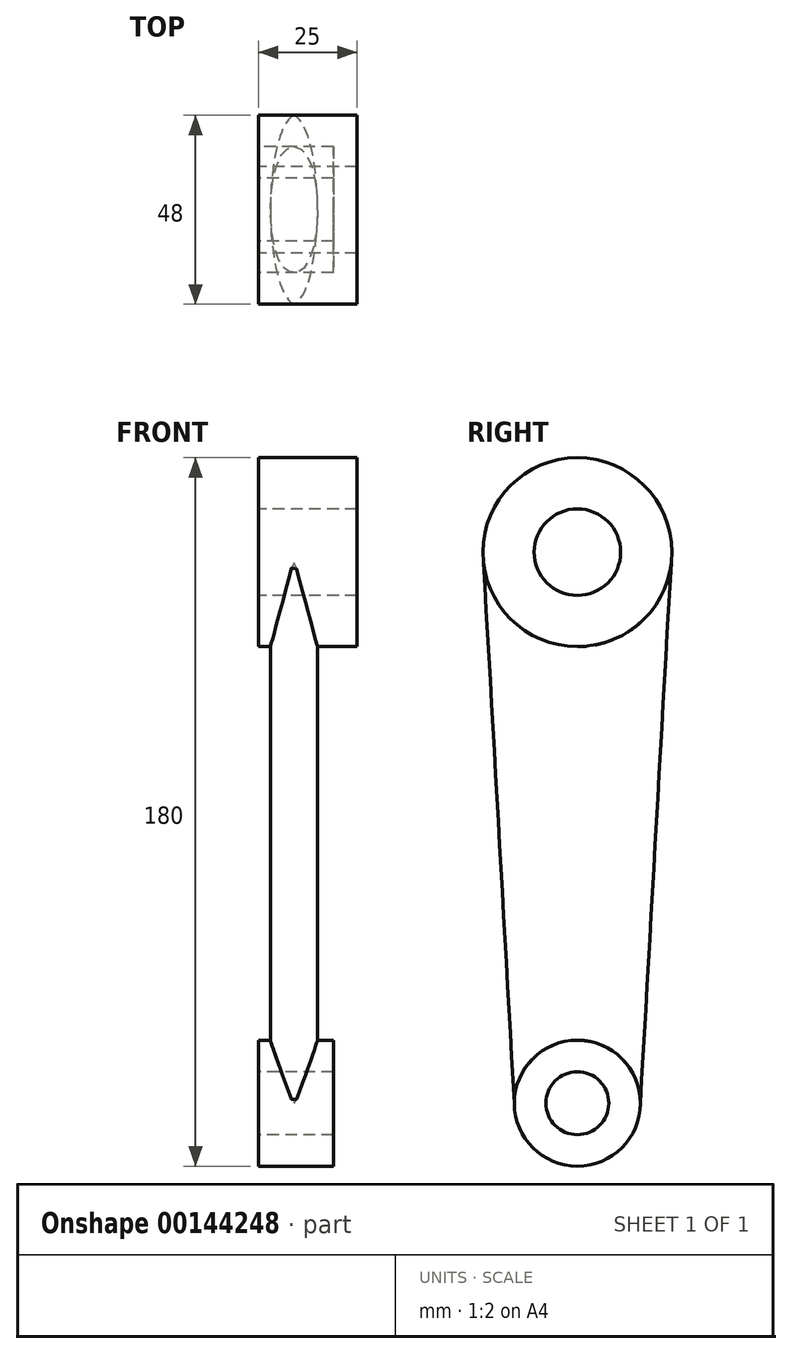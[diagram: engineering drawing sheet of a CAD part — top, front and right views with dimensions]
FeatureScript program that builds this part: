
annotation { "Feature Type Name" : "Feature", "Feature Type Description" : "" }
export const myFeature = defineFeature(function(context is Context, id is Id, definition is map)
    precondition{}
    {
        {
            var Q0;
            Q0=qCreatedBy(makeId("Right.planeOp"),FACE);
            var sketch = newSketch(context, id + "F0", { "sketchPlane" : qUnion([Q0])});
            skCircle(sketch, "E0", {"center": v(0, 0) * mm, "radius": 8 * mm});
            skCircle(sketch, "E1", {"center": v(0, 0) * mm, "radius": 16 * mm});
            skCircle(sketch, "E2", {"center": v(0, 140) * mm, "radius": 11 * mm});
            skCircle(sketch, "E3", {"center": v(0, 140) * mm, "radius": 24 * mm});
            skSolve(sketch);
        }
        {
            var Q0;
            Q0=makeQuery(id+"F0.imprint","IMPRINT",FACE,{"disambiguationData":[TD([[makeQuery(id+"F0.imprint","IMPRINT",EDGE,{"derivedFrom":sQuery(id+"F0.wireOp",EDGE,"E0")}),-1.0]])]});
            var Q1;
            Q1=makeQuery(id+"F0.imprint","IMPRINT",FACE,{"disambiguationData":[TD([[makeQuery(id+"F0.imprint","IMPRINT",EDGE,{"derivedFrom":sQuery(id+"F0.wireOp",EDGE,"E0")}),1.0]])]});
            extrude(context, id + "F1", {"entities" : qUnion([Q0, Q1]), "depth" : 19 * mm});
        }
        {
            var Q0;
            Q0=makeQuery(id+"F0.imprint","IMPRINT",FACE,{"disambiguationData":[TD([[makeQuery(id+"F0.imprint","IMPRINT",EDGE,{"derivedFrom":sQuery(id+"F0.wireOp",EDGE,"E2")}),-1.0]])]});
            var Q1;
            Q1=makeQuery(id+"F0.imprint","IMPRINT",FACE,{"disambiguationData":[TD([[makeQuery(id+"F0.imprint","IMPRINT",EDGE,{"derivedFrom":sQuery(id+"F0.wireOp",EDGE,"E2")}),1.0]])]});
            extrude(context, id + "F2", {"entities" : qUnion([Q0, Q1]), "operationType" : NewBodyOperationType.ADD, "depth" : 25 * mm});
        }
        {
            var Q0;
            Q0=qCreatedBy(makeId("Top.planeOp"),FACE);
            var sketch = newSketch(context, id + "F3", { "sketchPlane" : qUnion([Q0])});
            skEllipse(sketch, "E4", {"center": v(9, 0) * mm, "majorRadius": 16 * mm, "minorRadius": 6 * mm, "majorAxis": v(0, 1)});
            skPoint(sketch, "E5", {"position": v(3, 0) * mm});
            skLineSegment(sketch, "E6", {"start": v(0, 16) * mm, "end": v(19, 16) * mm, "construction": true});
            skSolve(sketch);
        }
        {
            var Q0;
            Q0=sQuery(id+"F0.wireOp",VERTEX,"E3.center");
            var Q1;
            Q1=qCreatedBy(makeId("Top.planeOp"),FACE);
            cPlane(context, id + "F4", {"entities" : qUnion([Q0, Q1]), "cplaneType" : CPlaneType.PLANE_POINT, "offset" : 25 * mm, "width" : 150 * mm, "height" : 150 * mm});
        }
        {
            var Q0;
            Q0=qCreatedBy(id+"F4.planeOp",FACE);
            var sketch = newSketch(context, id + "F5", { "sketchPlane" : qUnion([Q0])});
            skEllipse(sketch, "E7", {"center": v(9, 0) * mm, "majorRadius": 24 * mm, "minorRadius": 6 * mm, "majorAxis": v(0, 1)});
            skPoint(sketch, "E8", {"position": v(3, 0) * mm});
            skLineSegment(sketch, "E9", {"start": v(0, 24) * mm, "end": v(25, 24) * mm, "construction": true});
            skSolve(sketch);
        }
        {
            var Q0;
            Q0=makeQuery(id+"F5.imprint","IMPRINT",FACE,{"disambiguationData":[TD([[makeQuery(id+"F5.imprint","IMPRINT",EDGE,{"derivedFrom":sQuery(id+"F5.wireOp",EDGE,"E7")}),1.0]])]});
            var Q1;
            Q1=makeQuery(id+"F3.imprint","IMPRINT",FACE,{"disambiguationData":[TD([[makeQuery(id+"F3.imprint","IMPRINT",EDGE,{"derivedFrom":sQuery(id+"F3.wireOp",EDGE,"E4")}),1.0]])]});
            loft(context, id + "F6", {"operationType" : NewBodyOperationType.ADD, "sheetProfilesArray" : [{ "sheetProfileEntities" : qUnion([Q0]) }, { "sheetProfileEntities" : qUnion([Q1]) }]});
        }
        {
            var Q0;
            Q0=makeQuery(id+"F0.imprint","IMPRINT",FACE,{"disambiguationData":[TD([[makeQuery(id+"F0.imprint","IMPRINT",EDGE,{"derivedFrom":sQuery(id+"F0.wireOp",EDGE,"E2")}),1.0]])]});
            var Q1;
            Q1=makeQuery(id+"F0.imprint","IMPRINT",FACE,{"disambiguationData":[TD([[makeQuery(id+"F0.imprint","IMPRINT",EDGE,{"derivedFrom":sQuery(id+"F0.wireOp",EDGE,"E0")}),1.0]])]});
            extrude(context, id + "F7", {"entities" : qUnion([Q0, Q1]), "operationType" : NewBodyOperationType.REMOVE, "endBound" : BoundingType.THROUGH_ALL, "depth" : 25 * mm});
        }
    });
